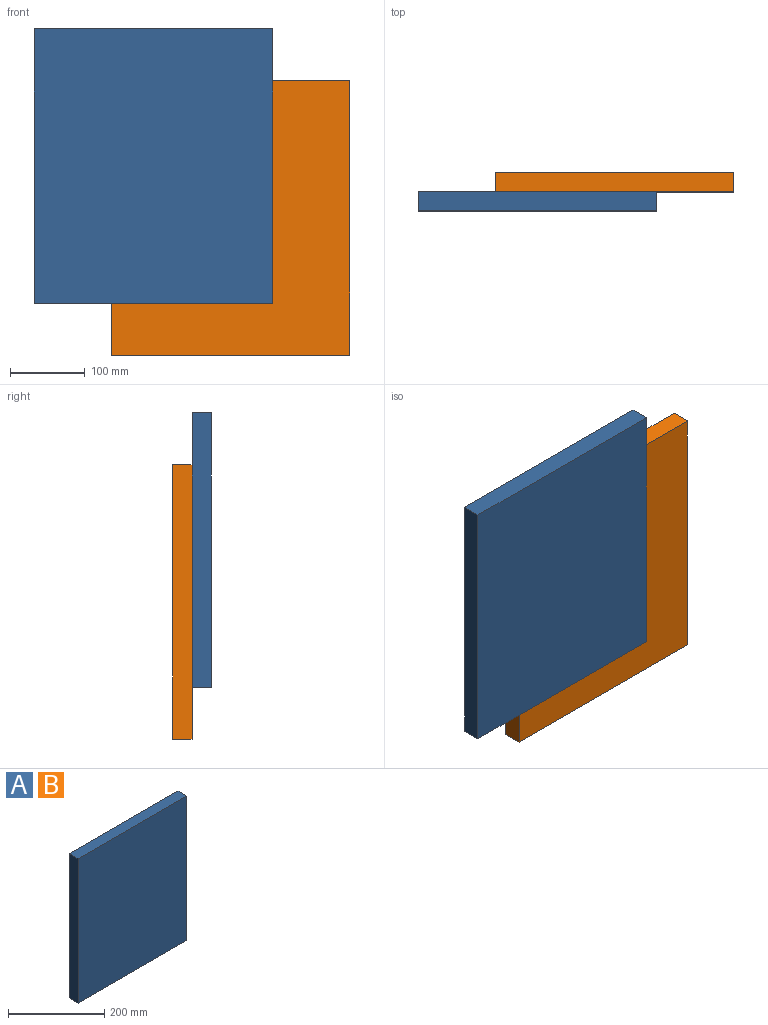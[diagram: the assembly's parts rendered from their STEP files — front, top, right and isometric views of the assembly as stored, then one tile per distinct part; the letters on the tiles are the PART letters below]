
ASSEMBLY  parts=2 mates=1
PART A: 6 faces, bbox 318.5x25.4x366.4 mm
  f0: plane 366.36x25.4mm, normal (-1,0,0), area 9305.6mm2, adj f1,f3,f4,f5
  f1: plane 318.48x25.4mm, normal (0,0,-1), area 8089.4mm2, adj f0,f2,f4,f5
  f2: plane 366.36x25.4mm, normal (1,0,0), area 9305.6mm2, adj f1,f3,f4,f5
  f3: plane 318.48x25.4mm, normal (0,0,1), area 8089.4mm2, adj f0,f2,f4,f5
  f4: plane 366.36x318.48mm, normal (0,-1,0), area 116679.2mm2, adj f0,f1,f2,f3
  f5: plane 366.36x318.48mm, normal (0,1,0), area 116679.2mm2, adj f0,f1,f2,f3
PART B: same geometry as A
PLACE A t=(-282.71,-230.4,15.62)mm
PLACE B t=(-179.65,-205,-53.83)mm
MATE planar A.f5 <-> B.f4  axis (0,1,0) through (-227.93,-230.4,-14.48)mm
